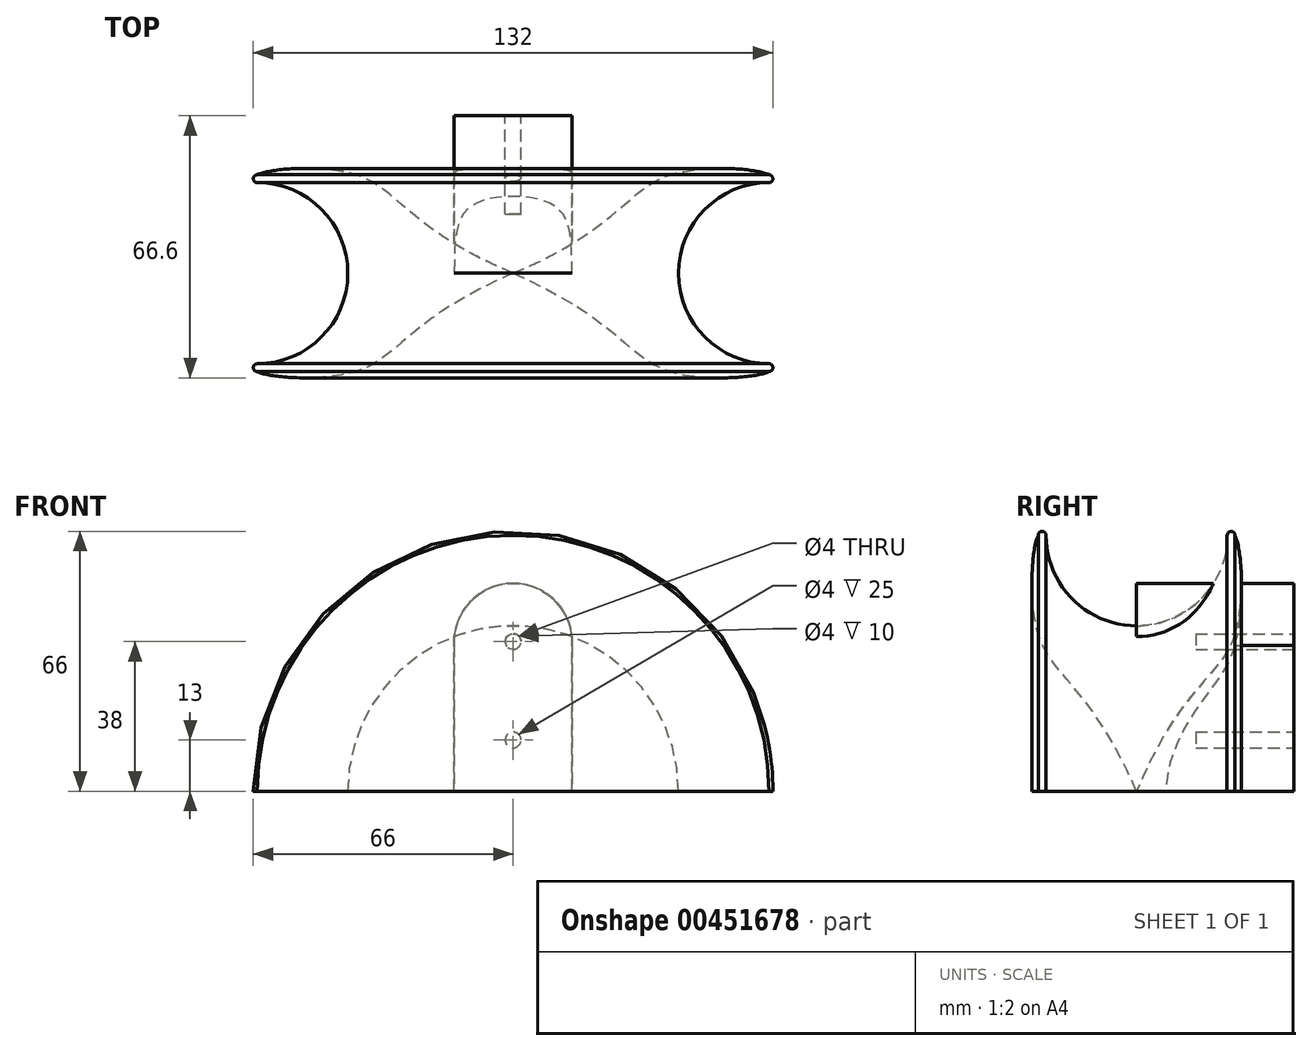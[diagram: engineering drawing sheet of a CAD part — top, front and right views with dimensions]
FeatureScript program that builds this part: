
annotation { "Feature Type Name" : "Feature", "Feature Type Description" : "" }
export const myFeature = defineFeature(function(context is Context, id is Id, definition is map)
    precondition{}
    {
        {
            var Q0;
            Q0=qCreatedBy(makeId("Front.planeOp"),FACE);
            var sketch = newSketch(context, id + "F0", { "sketchPlane" : qUnion([Q0])});
            skArc(sketch, "E0", {"start": v(-40, 0) * mm, "mid": v(0, 40) * mm, "end": v(40, 0) * mm});
            skSolve(sketch);
        }
        {
            var Q0;
            Q0=qCreatedBy(makeId("Top.planeOp"),FACE);
            var sketch = newSketch(context, id + "F1", { "sketchPlane" : qUnion([Q0])});
            skPoint(sketch, "E1.first.point", {"position": v(40, 0) * mm});
            skPoint(sketch, "E1.third.point", {"position": v(65, 25) * mm});
            skArc(sketch, "E2", {"start": v(65, 25) * mm, "mid": v(40, 0) * mm, "end": v(65, -25) * mm});
            skArc(sketch, "E3.0", {"start": v(65, 23) * mm, "mid": v(42, 0) * mm, "end": v(65, -23) * mm});
            skArc(sketch, "E4", {"start": v(65, 23) * mm, "mid": v(66, 24) * mm, "end": v(65, 25) * mm});
            skArc(sketch, "E5", {"start": v(65, -23) * mm, "mid": v(66, -24) * mm, "end": v(65, -25) * mm});
            skLineSegment(sketch, "E6", {"start": v(40, 0) * mm, "end": v(40, -25) * mm, "construction": true});
            skLineSegment(sketch, "E7", {"start": v(40, 0) * mm, "end": v(40, 25) * mm, "construction": true});
            skFitSpline(sketch, "E8", {"points": [v(0, 0) * mm, v(40, -25) * mm, v(65, -25) * mm], "startDerivative": vector(141.36, -61.65) * mm, "endDerivative": vector(25.06, 12.2) * mm});
            skFitSpline(sketch, "E9", {"points": [v(0, 0) * mm, v(40, 25) * mm, v(65, 25) * mm], "startDerivative": vector(141.36, 59.31) * mm, "endDerivative": vector(25.06, -12.35) * mm});
            skSolve(sketch);
        }
        {
            var Q0;
            Q0 = qSketchRegion(id + "F1", true);
            var Q1;
            Q1 = qConstructionFilter(qBodyType(qCreatedBy(id + "F0" ,EDGE), BodyType.WIRE), ConstructionObject.NO);
            sweep(context, id + "F2", {"profiles" : qUnion([Q0]), "path" : qUnion([Q1])});
        }
        {
            var Q0;
            Q0=qCreatedBy(makeId("Front.planeOp"),FACE);
            cPlane(context, id + "F3", {"entities" : qUnion([Q0]), "cplaneType" : CPlaneType.OFFSET, "offset" : 40 * mm, "oppositeDirection" : true, "width" : 150 * mm, "height" : 150 * mm});
        }
        {
            var Q0;
            Q0=qCreatedBy(id+"F3.planeOp",FACE);
            var sketch = newSketch(context, id + "F4", { "sketchPlane" : qUnion([Q0])});
            skLineSegment(sketch, "E10", {"start": v(0, 0) * mm, "end": v(15, 0) * mm});
            skLineSegment(sketch, "E11", {"start": v(15, 0) * mm, "end": v(15, 37) * mm});
            skLineSegment(sketch, "E12.MirrorCS", {"start": v(0, 0) * mm, "end": v(-15, 0) * mm});
            skLineSegment(sketch, "E13.MirrorCS", {"start": v(-15, 0) * mm, "end": v(-15, 37) * mm});
            skArc(sketch, "E14", {"start": v(15, 37) * mm, "mid": v(0, 52.81) * mm, "end": v(-15, 37) * mm});
            skLineSegment(sketch, "E15", {"start": v(15, 37) * mm, "end": v(-15, 37) * mm});
            skSolve(sketch);
        }
        {
            var Q0;
            Q0=makeQuery(id+"F4.imprint","IMPRINT",FACE,{"disambiguationData":[TD([[makeQuery(id+"F4.imprint","IMPRINT",EDGE,{"derivedFrom":sQuery(id+"F4.wireOp",EDGE,"E10")}),1.0]])]});
            var Q1;
            Q1=makeQuery(id+"F4.imprint","IMPRINT",FACE,{"disambiguationData":[TD([[makeQuery(id+"F4.imprint","IMPRINT",EDGE,{"derivedFrom":sQuery(id+"F4.wireOp",EDGE,"E14")}),1.0]])]});
            var Q2;
            Q2=qCreatedBy(makeId("Origin.pointOp"),VERTEX);
            extrude(context, id + "F5", {"entities" : qUnion([Q0, Q1]), "endBound" : BoundingType.UP_TO_VERTEX, "endBoundEntityVertex" : qUnion([Q2]), "depth" : 25 * mm});
        }
        {
            var Q0;
            Q0=makeQuery(id+"F2.opSweep","SWEPT_BODY",BODY,{"disambiguationData":[OSD([sQuery(id+"F0.wireOp",EDGE,"E0"),sQuery(id+"F1.wireOp",EDGE,"ff895426-1113-4e85-9941-420be04735441"),sQuery(id+"F1.wireOp",EDGE,"67b6ee90-f6e3-4ef7-b274-51db0571cec1.0"),sQuery(id+"F1.wireOp",EDGE,"c4e20f14-ed8d-4cd4-abd5-5c01eb1e0884"),sQuery(id+"F1.wireOp",EDGE,"b505eb6f-637c-4d00-bb4e-f6435f0b95e1"),sQuery(id+"F1.wireOp",EDGE,"d775dc81-7d78-49f9-9f7b-2835cde1460f"),sQuery(id+"F1.wireOp",EDGE,"a09ba10a-9758-4753-b996-148cd820c5930.MirrorCS")])]});
            transform(context, id + "F6", {"entities" : qUnion([Q0]), "transformType" : TransformType.TRANSLATION_3D, "dx" : 0 * mm, "dy" : 0 * mm, "dz" : 0 * mm, "makeCopy" : true});
        }
        {
            var Q0;
            Q0=makeQuery(id+"F2.opSweep","SWEPT_BODY",BODY,{"disambiguationData":[OSD([sQuery(id+"F0.wireOp",EDGE,"E0"),sQuery(id+"F1.wireOp",EDGE,"ff895426-1113-4e85-9941-420be04735441"),sQuery(id+"F1.wireOp",EDGE,"67b6ee90-f6e3-4ef7-b274-51db0571cec1.0"),sQuery(id+"F1.wireOp",EDGE,"c4e20f14-ed8d-4cd4-abd5-5c01eb1e0884"),sQuery(id+"F1.wireOp",EDGE,"b505eb6f-637c-4d00-bb4e-f6435f0b95e1"),sQuery(id+"F1.wireOp",EDGE,"d775dc81-7d78-49f9-9f7b-2835cde1460f"),sQuery(id+"F1.wireOp",EDGE,"a09ba10a-9758-4753-b996-148cd820c5930.MirrorCS")])]});
            var Q1;
            Q1=makeQuery(id+"F5.opExtrude","SWEPT_BODY",BODY,{"disambiguationData":[OSD([sQuery(id+"F4.wireOp",EDGE,"E10"),sQuery(id+"F4.wireOp",EDGE,"E11"),sQuery(id+"F4.wireOp",EDGE,"E12.MirrorCS"),sQuery(id+"F4.wireOp",EDGE,"E13.MirrorCS"),sQuery(id+"F4.wireOp",EDGE,"E14")])]});
            booleanBodies(context, id + "F7", {"operationType" : BooleanOperationType.SUBTRACTION, "tools" : qUnion([Q0]), "targets" : qUnion([Q1])});
        }
        {
            var Q0;
            Q0=makeQuery(id+"F5.opExtrude","CAP_FACE",FACE,{"disambiguationData":[OSD([sQuery(id+"F4.wireOp",EDGE,"E10"),sQuery(id+"F4.wireOp",EDGE,"E11"),sQuery(id+"F4.wireOp",EDGE,"E12.MirrorCS"),sQuery(id+"F4.wireOp",EDGE,"E13.MirrorCS"),sQuery(id+"F4.wireOp",EDGE,"E14")])],"isStart":true});
            var sketch = newSketch(context, id + "F8", { "sketchPlane" : qUnion([Q0])});
            skLineSegment(sketch, "E16", {"start": v(0, 13) * mm, "end": v(0, 38) * mm, "construction": true});
            skCircle(sketch, "E17", {"center": v(0, 38) * mm, "radius": 2 * mm});
            skCircle(sketch, "E18", {"center": v(0, 13) * mm, "radius": 2 * mm});
            skSolve(sketch);
        }
        {
            var Q0;
            Q0=makeQuery(id+"F8.imprint","IMPRINT",FACE,{"disambiguationData":[TD([[makeQuery(id+"F8.imprint","IMPRINT",EDGE,{"derivedFrom":sQuery(id+"F8.wireOp",EDGE,"E17")}),1.0]])]});
            var Q1;
            Q1=makeQuery(id+"F8.imprint","IMPRINT",FACE,{"disambiguationData":[TD([[makeQuery(id+"F8.imprint","IMPRINT",EDGE,{"derivedFrom":sQuery(id+"F8.wireOp",EDGE,"E18")}),1.0]])]});
            extrude(context, id + "F9", {"entities" : qUnion([Q0, Q1]), "operationType" : NewBodyOperationType.REMOVE, "oppositeDirection" : true, "depth" : 25 * mm});
        }
    });
